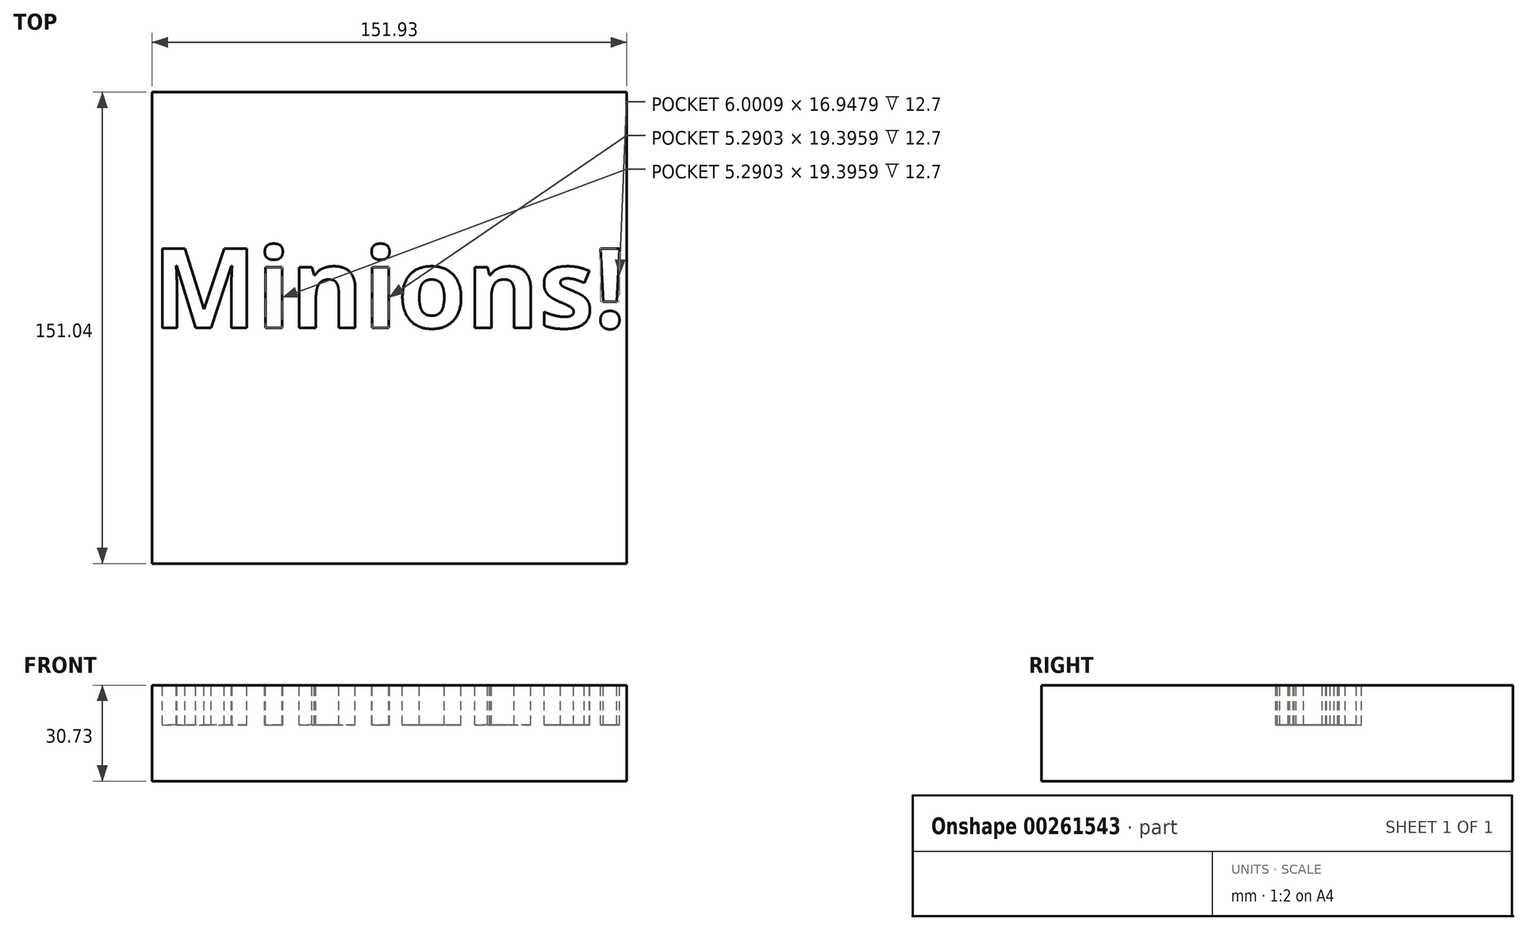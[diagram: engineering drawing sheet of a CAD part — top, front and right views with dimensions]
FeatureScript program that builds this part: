
annotation { "Feature Type Name" : "Feature", "Feature Type Description" : "" }
export const myFeature = defineFeature(function(context is Context, id is Id, definition is map)
    precondition{}
    {
        {
            var Q0;
            Q0=qCreatedBy(makeId("Top.planeOp"),FACE);
            var sketch = newSketch(context, id + "F0", { "sketchPlane" : qUnion([Q0])});
            skLineSegment(sketch, "E0.bottom", {"start": v(-76.2, 76.34) * mm, "end": v(75.73, 76.34) * mm});
            skLineSegment(sketch, "E0.top", {"start": v(-76.2, -74.7) * mm, "end": v(75.73, -74.7) * mm});
            skLineSegment(sketch, "E0.left", {"start": v(-76.2, 76.34) * mm, "end": v(-76.2, -74.7) * mm});
            skLineSegment(sketch, "E0.right", {"start": v(75.73, 76.34) * mm, "end": v(75.73, -74.7) * mm});
            skSolve(sketch);
        }
        {
            var Q0;
            Q0=makeQuery(id+"F0.imprint","IMPRINT",FACE,{"disambiguationData":[TD([[makeQuery(id+"F0.imprint","IMPRINT",EDGE,{"derivedFrom":sQuery(id+"F0.wireOp",EDGE,"E0.bottom")}),-1.0]])]});
            extrude(context, id + "F1", {"entities" : qUnion([Q0]), "depth" : 30.73 * mm});
        }
        {
            var Q0;
            Q0=makeQuery(id+"F1.opExtrude","CAP_FACE",FACE,{"disambiguationData":[OSD([sQuery(id+"F0.wireOp",EDGE,"E0.bottom"),sQuery(id+"F0.wireOp",EDGE,"E0.top"),sQuery(id+"F0.wireOp",EDGE,"E0.left"),sQuery(id+"F0.wireOp",EDGE,"E0.right")])],"isStart":false});
            var sketch = newSketch(context, id + "F2", { "sketchPlane" : qUnion([Q0])});
            skText(sketch, "E1", { "text": "Minions!", "fontName": "OpenSans-Bold.ttf"});
            const initialGuessF2  = {"E1": [-0.0762, 0.00082, 1, 0, 0.02558]};
            skSetInitialGuess(sketch, initialGuessF2);
            skSolve(sketch);
        }
        {
            var Q0;
            Q0 = qSketchRegion(id + "F2", true);
            extrude(context, id + "F3", {"entities" : qUnion([Q0]), "operationType" : NewBodyOperationType.REMOVE, "oppositeDirection" : true, "depth" : 12.7 * mm});
        }
    });
